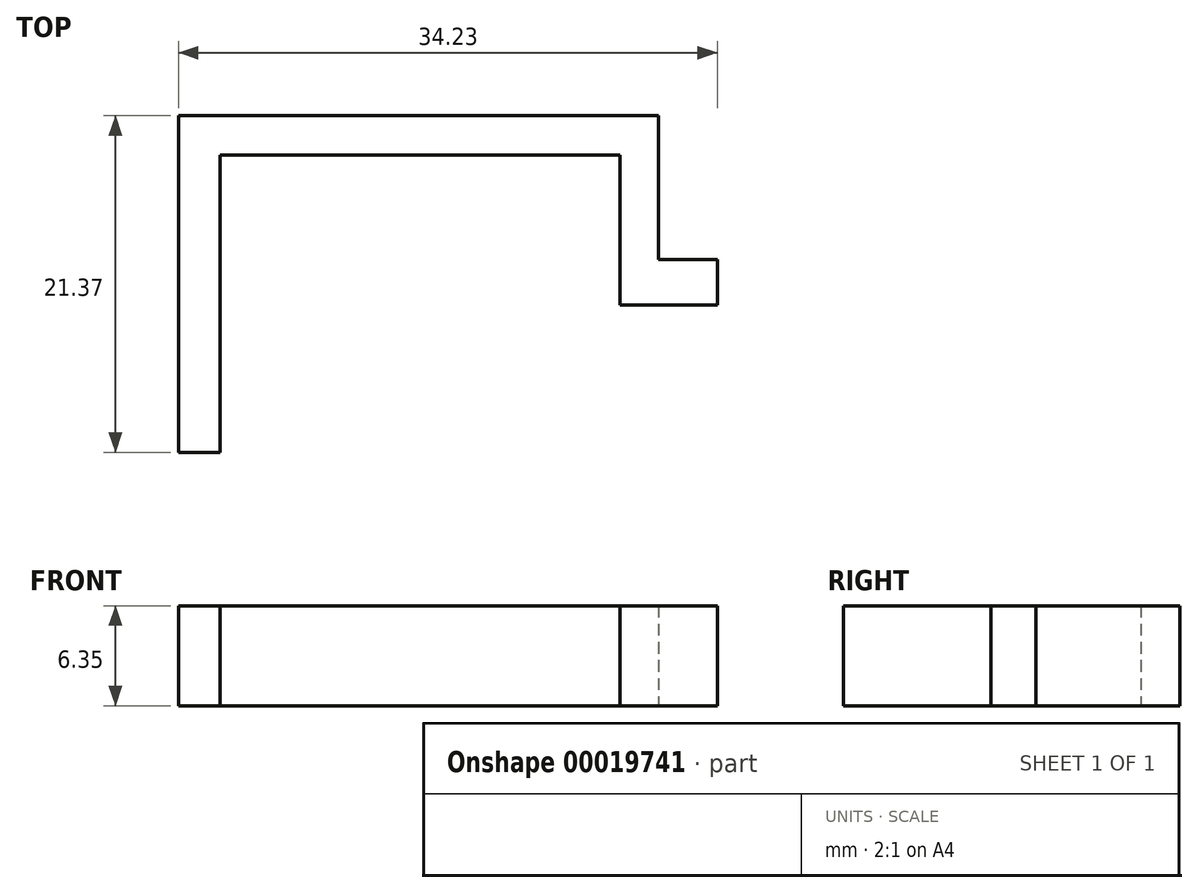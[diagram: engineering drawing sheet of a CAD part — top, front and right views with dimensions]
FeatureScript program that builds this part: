
annotation { "Feature Type Name" : "Feature", "Feature Type Description" : "" }
export const myFeature = defineFeature(function(context is Context, id is Id, definition is map)
    precondition{}
    {
        {
            var Q0;
            Q0=qCreatedBy(makeId("Top.planeOp"),FACE);
            var sketch = newSketch(context, id + "F0", { "sketchPlane" : qUnion([Q0])});
            skLineSegment(sketch, "E0", {"start": v(-14.8, -4.72) * mm, "end": v(-14.8, 16.65) * mm});
            skLineSegment(sketch, "E1", {"start": v(15.68, 16.65) * mm, "end": v(15.68, 7.51) * mm});
            skLineSegment(sketch, "E2", {"start": v(15.68, 7.51) * mm, "end": v(19.43, 7.51) * mm});
            skLineSegment(sketch, "E3", {"start": v(19.43, 7.51) * mm, "end": v(19.43, 4.65) * mm});
            skLineSegment(sketch, "E4", {"start": v(19.43, 4.65) * mm, "end": v(13.24, 4.65) * mm});
            skLineSegment(sketch, "E5", {"start": v(13.24, 0) * mm, "end": v(13.24, 4.65) * mm});
            skLineSegment(sketch, "E6", {"start": v(-12.16, 14.17) * mm, "end": v(-12.16, -4.72) * mm});
            skLineSegment(sketch, "E7", {"start": v(-12.16, -4.72) * mm, "end": v(-14.8, -4.72) * mm});
            skLineSegment(sketch, "E8", {"start": v(13.24, 0) * mm, "end": v(13.24, 14.17) * mm});
            skLineSegment(sketch, "E9", {"start": v(-14.8, 16.65) * mm, "end": v(15.68, 16.65) * mm});
            skLineSegment(sketch, "E10", {"start": v(-12.16, 14.17) * mm, "end": v(13.24, 14.17) * mm});
            skLineSegment(sketch, "E11", {"start": v(-12.16, -2.5) * mm, "end": v(13.24, -2.9) * mm, "construction": true});
            skSolve(sketch);
        }
        {
            var Q0;
            Q0=makeQuery(id+"F0.imprint","IMPRINT",FACE,{"disambiguationData":[TD([[makeQuery(id+"F0.imprint","IMPRINT",EDGE,{"derivedFrom":sQuery(id+"F0.wireOp",EDGE,"E0")}),-1.0]])]});
            extrude(context, id + "F1", {"entities" : qUnion([Q0]), "depth" : 6.35 * mm});
        }
    });
